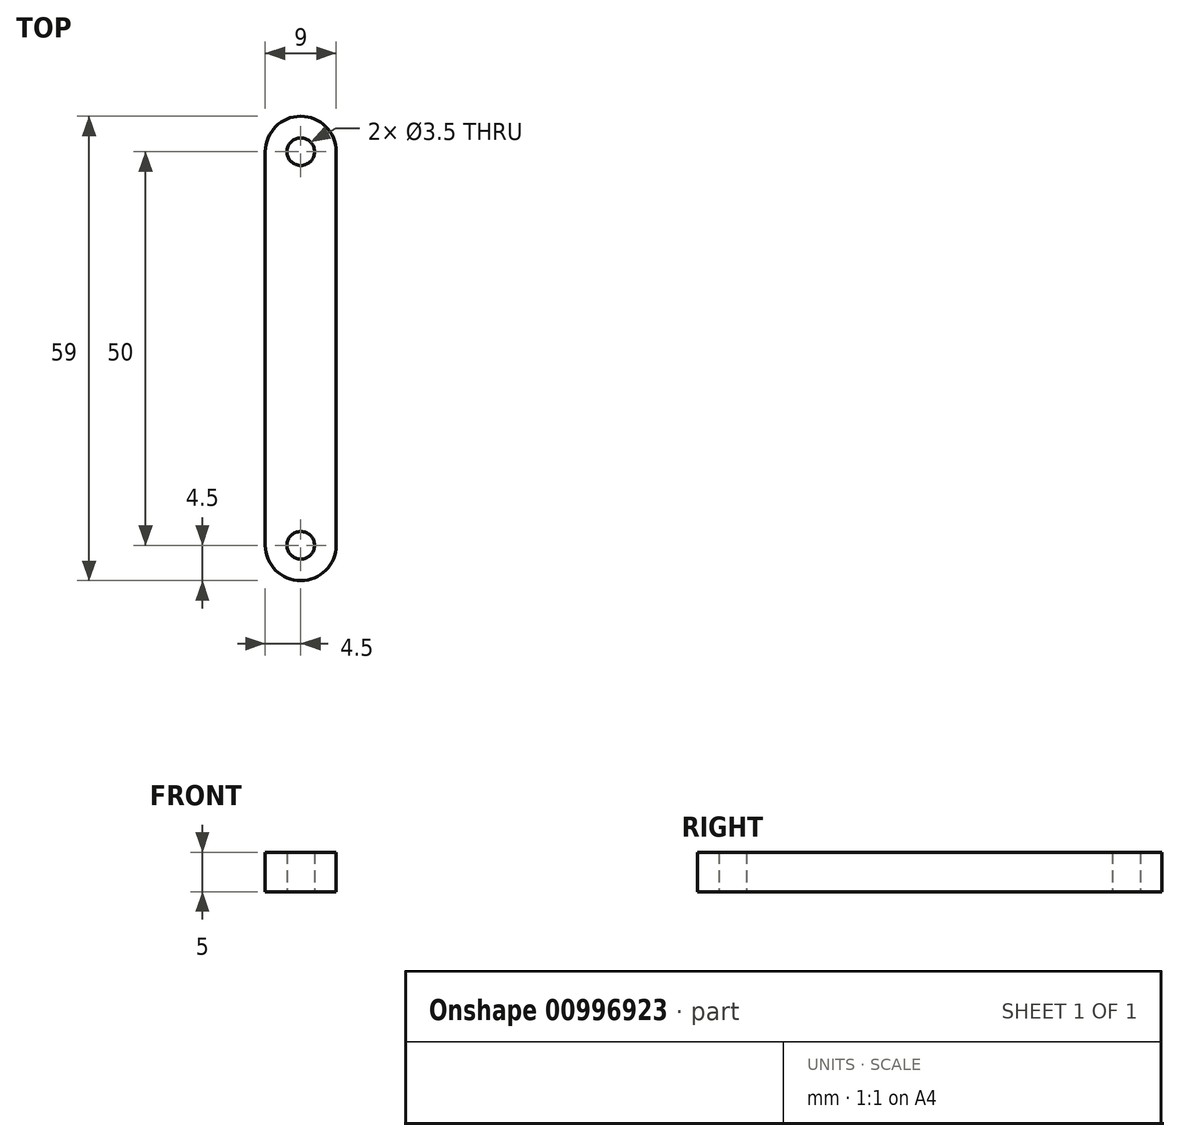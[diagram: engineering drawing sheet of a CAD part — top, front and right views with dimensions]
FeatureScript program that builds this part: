
annotation { "Feature Type Name" : "Feature", "Feature Type Description" : "" }
export const myFeature = defineFeature(function(context is Context, id is Id, definition is map)
    precondition{}
    {
        {
            var Q0;
            Q0=qCreatedBy(makeId("Top.planeOp"),FACE);
            var sketch = newSketch(context, id + "F0", { "sketchPlane" : qUnion([Q0])});
            skCircle(sketch, "E0", {"center": v(0, 0) * mm, "radius": 1.75 * mm});
            skCircle(sketch, "E1", {"center": v(0, 50) * mm, "radius": 1.75 * mm});
            skArc(sketch, "E2", {"start": v(-4.5, 0) * mm, "mid": v(0, -4.5) * mm, "end": v(4.5, 0) * mm});
            skArc(sketch, "E3", {"start": v(4.5, 50) * mm, "mid": v(0, 54.5) * mm, "end": v(-4.5, 50) * mm});
            skLineSegment(sketch, "E4", {"start": v(-4.5, 50) * mm, "end": v(-4.5, 0) * mm});
            skLineSegment(sketch, "E5", {"start": v(4.5, 50) * mm, "end": v(4.5, 0) * mm});
            skSolve(sketch);
        }
        {
            var Q0;
            Q0 = qSketchRegion(id + "F0", true);
            extrude(context, id + "F1", {"entities" : qUnion([Q0]), "depth" : 5 * mm, "offsetDistance" : 25 * mm});
        }
    });
